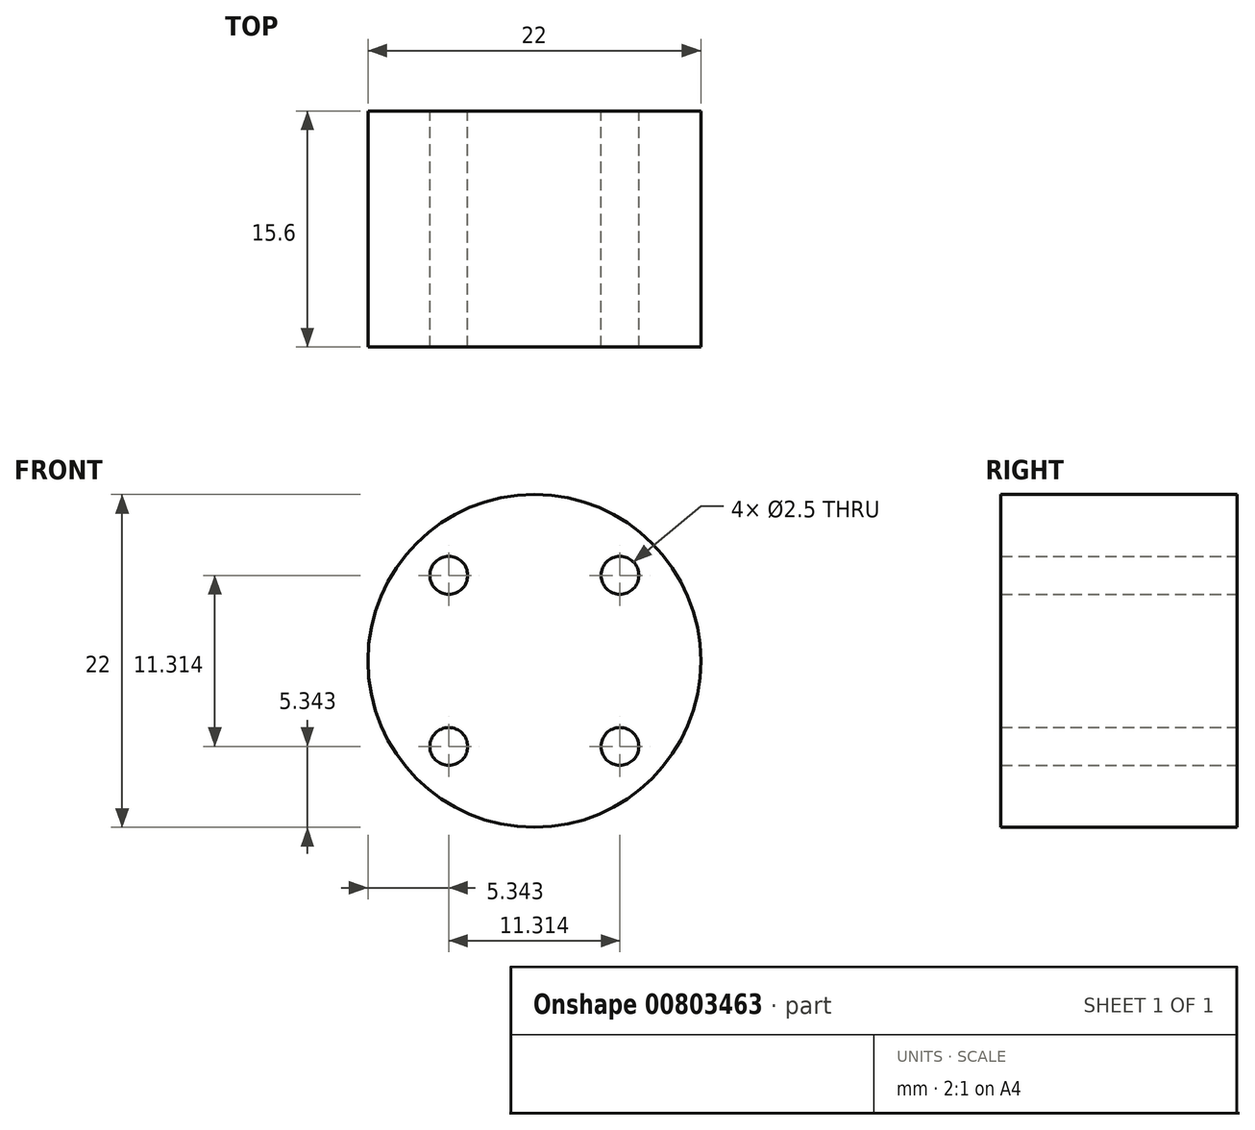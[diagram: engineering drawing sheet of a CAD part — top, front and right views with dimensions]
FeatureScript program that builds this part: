
annotation { "Feature Type Name" : "Feature", "Feature Type Description" : "" }
export const myFeature = defineFeature(function(context is Context, id is Id, definition is map)
    precondition{}
    {
        {
            var Q0;
            Q0=qCreatedBy(makeId("Front.planeOp"),FACE);
            var sketch = newSketch(context, id + "F0", { "sketchPlane" : qUnion([Q0])});
            skCircle(sketch, "E0", {"center": v(0, 0) * mm, "radius": 11 * mm});
            skLineSegment(sketch, "E1", {"start": v(0, 29.65) * mm, "end": v(0, -28.8) * mm, "construction": true});
            skLineSegment(sketch, "E2", {"start": v(-6.72, 6.72) * mm, "end": v(4.6, -4.6) * mm, "construction": true});
            skCircle(sketch, "E3", {"center": v(-5.66, 5.66) * mm, "radius": 1.25 * mm});
            skCircle(sketch, "E4.MirrorC", {"center": v(5.66, 5.66) * mm, "radius": 1.25 * mm});
            skCircle(sketch, "E5.MirrorC", {"center": v(5.66, -5.66) * mm, "radius": 1.25 * mm});
            skCircle(sketch, "E6.MirrorC", {"center": v(-5.66, -5.66) * mm, "radius": 1.25 * mm});
            skSolve(sketch);
        }
        {
            var Q0;
            Q0=makeQuery(id+"F0.imprint","IMPRINT",FACE,{"disambiguationData":[TD([[makeQuery(id+"F0.imprint","IMPRINT",EDGE,{"derivedFrom":sQuery(id+"F0.wireOp",EDGE,"E0")}),1.0]])]});
            extrude(context, id + "F1", {"entities" : qUnion([Q0]), "depth" : 15.6 * mm, "offsetDistance" : 25 * mm});
        }
    });
